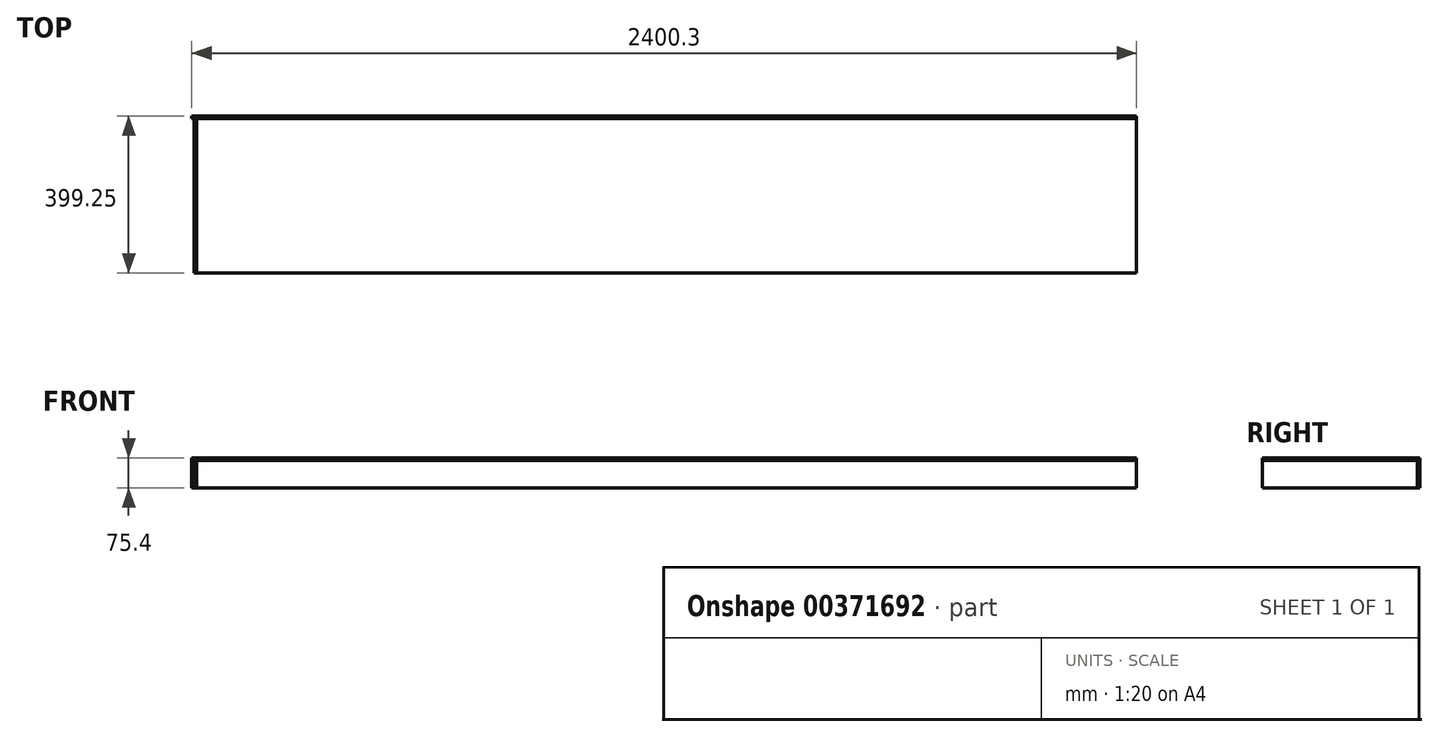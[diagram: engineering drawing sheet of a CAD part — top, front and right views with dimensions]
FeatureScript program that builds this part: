
annotation { "Feature Type Name" : "Feature", "Feature Type Description" : "" }
export const myFeature = defineFeature(function(context is Context, id is Id, definition is map)
    precondition{}
    {
        {
            var Q0;
            Q0=qCreatedBy(makeId("Top.planeOp"),FACE);
            var sketch = newSketch(context, id + "F0", { "sketchPlane" : qUnion([Q0])});
            skLineSegment(sketch, "E0.bottom", {"start": v(-1193.8, 196.45) * mm, "end": v(1193.8, 196.45) * mm});
            skLineSegment(sketch, "E0.top", {"start": v(-1193.8, -196.45) * mm, "end": v(1193.8, -196.45) * mm});
            skLineSegment(sketch, "E0.left", {"start": v(-1193.8, 196.45) * mm, "end": v(-1193.8, -196.45) * mm});
            skLineSegment(sketch, "E0.right", {"start": v(1193.8, 196.45) * mm, "end": v(1193.8, -196.45) * mm});
            skPoint(sketch, "E0.middle", {"position": v(0, 0) * mm});
            skSolve(sketch);
        }
        {
            var Q0;
            Q0=makeQuery(id+"F0.imprint","IMPRINT",FACE,{"disambiguationData":[TD([[makeQuery(id+"F0.imprint","IMPRINT",EDGE,{"derivedFrom":sQuery(id+"F0.wireOp",EDGE,"E0.bottom")}),-1.0]])]});
            extrude(context, id + "F1", {"entities" : qUnion([Q0]), "depth" : 6.35 * mm});
        }
        {
            var Q0;
            Q0=makeQuery(id+"F1.opExtrude","SWEPT_FACE",FACE,{"disambiguationData":[OSD([sQuery(id+"F0.wireOp",EDGE,"E0.left")])]});
            var sketch = newSketch(context, id + "F2", { "sketchPlane" : qUnion([Q0])});
            skLineSegment(sketch, "E1.bottom", {"start": v(-196.45, 6.35) * mm, "end": v(196.45, 6.35) * mm});
            skLineSegment(sketch, "E1.top", {"start": v(-196.45, -69.05) * mm, "end": v(196.45, -69.05) * mm});
            skLineSegment(sketch, "E1.left", {"start": v(-196.45, 6.35) * mm, "end": v(-196.45, -69.05) * mm});
            skLineSegment(sketch, "E1.right", {"start": v(196.45, 6.35) * mm, "end": v(196.45, -69.05) * mm});
            skSolve(sketch);
        }
        {
            var Q0;
            {var subQ0=sQuery(id+"F2.wireOp",EDGE,"E1.top");Q0=makeQuery(id+"F2.imprint","IMPRINT",FACE,{"disambiguationData":[TD([[makeQuery(id+"F2.imprint","IMPRINT",EDGE,{"derivedFrom":subQ0}),1.0]])]});}
            var Q1;
            {var subQ0=sQuery(id+"F2.wireOp",EDGE,"E1.bottom");Q1=makeQuery(id+"F2.imprint","IMPRINT",FACE,{"disambiguationData":[TD([[makeQuery(id+"F2.imprint","IMPRINT",EDGE,{"derivedFrom":subQ0}),-1.0]])]});}
            extrude(context, id + "F3", {"entities" : qUnion([Q0, Q1]), "depth" : 6.35 * mm});
        }
        {
            var Q0;
            Q0=makeQuery(id+"F1.opExtrude","SWEPT_FACE",FACE,{"disambiguationData":[OSD([sQuery(id+"F0.wireOp",EDGE,"E0.bottom")])]});
            var sketch = newSketch(context, id + "F4", { "sketchPlane" : qUnion([Q0])});
            skLineSegment(sketch, "E2.bottom", {"start": v(-1193.8, 6.35) * mm, "end": v(1206.5, 6.35) * mm});
            skLineSegment(sketch, "E2.top", {"start": v(-1193.8, -69.05) * mm, "end": v(1206.5, -69.05) * mm});
            skLineSegment(sketch, "E2.left", {"start": v(-1193.8, 6.35) * mm, "end": v(-1193.8, -69.05) * mm});
            skLineSegment(sketch, "E2.right", {"start": v(1206.5, 6.35) * mm, "end": v(1206.5, -69.05) * mm});
            skSolve(sketch);
        }
        {
            var Q0;
            {var subQ1=sQuery(id+"F0.wireOp",EDGE,"E0.bottom");var subQ5=makeQuery(id+"F1.opExtrude","CAP_EDGE",EDGE,{"disambiguationData":[OSD([subQ1])],"isStart":true});Q0=makeQuery(id+"F4.imprint","IMPRINT",FACE,{"disambiguationData":[TD([[makeQuery(id+"F4.imprint","IMPRINT",EDGE,{"derivedFrom":subQ5}),-1.0]])]});}
            var Q1;
            {var subQ4=sQuery(id+"F4.wireOp",EDGE,"E2.top");Q1=makeQuery(id+"F4.imprint","IMPRINT",FACE,{"disambiguationData":[TD([[makeQuery(id+"F4.imprint","IMPRINT",EDGE,{"derivedFrom":subQ4}),1.0]])]});}
            extrude(context, id + "F5", {"entities" : qUnion([Q0, Q1]), "depth" : 6.35 * mm});
        }
    });
